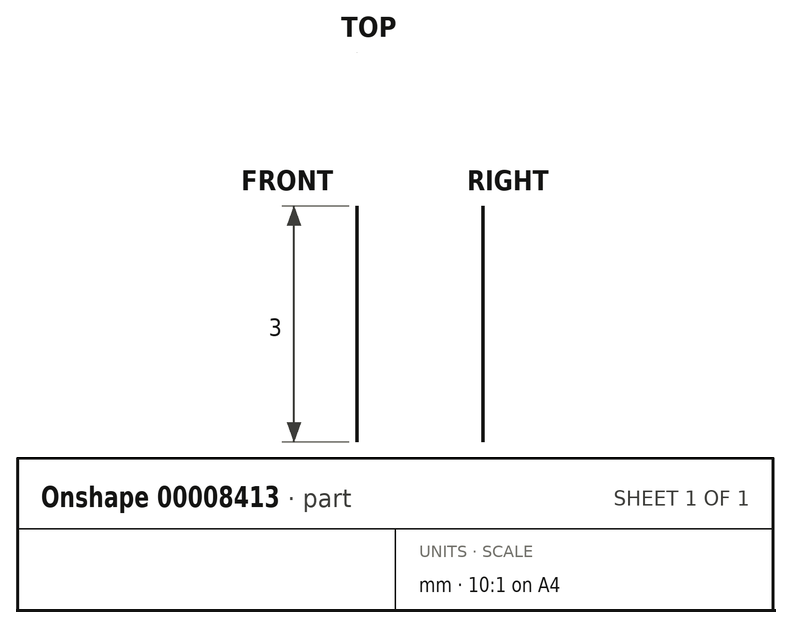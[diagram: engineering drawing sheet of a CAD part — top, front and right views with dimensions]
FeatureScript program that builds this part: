
annotation { "Feature Type Name" : "Feature", "Feature Type Description" : "" }
export const myFeature = defineFeature(function(context is Context, id is Id, definition is map)
    precondition{}
    {
        {
            var Q0;
            Q0=qCreatedBy(makeId("Top.planeOp"),FACE);
            var sketch = newSketch(context, id + "F0", { "sketchPlane" : qUnion([Q0])});
            skLineSegment(sketch, "E0.bottom", {"start": v(0, 0.5) * mm, "end": v(5.1, 0.5) * mm});
            skLineSegment(sketch, "E0.top", {"start": v(0, -0.5) * mm, "end": v(5.1, -0.5) * mm});
            skLineSegment(sketch, "E0.left", {"start": v(0, 0.5) * mm, "end": v(0, -0.5) * mm});
            skPoint(sketch, "E1", {"position": v(5.6, 0) * mm});
            skLineSegment(sketch, "E2", {"start": v(5.6, 1) * mm, "end": v(5.6, 1) * mm});
            skLineSegment(sketch, "E3", {"start": v(6.1, 1.5) * mm, "end": v(9.69, 1.5) * mm});
            skLineSegment(sketch, "E4", {"start": v(9.94, 1.25) * mm, "end": v(9.94, 0.75) * mm});
            skLineSegment(sketch, "E5", {"start": v(9.69, 0.5) * mm, "end": v(7.19, 0.5) * mm});
            skLineSegment(sketch, "E6", {"start": v(6.94, 0.25) * mm, "end": v(6.94, -0.25) * mm});
            skLineSegment(sketch, "E7", {"start": v(7.19, -0.5) * mm, "end": v(9.69, -0.5) * mm});
            skLineSegment(sketch, "E8", {"start": v(9.94, -0.75) * mm, "end": v(9.94, -1.25) * mm});
            skLineSegment(sketch, "E9", {"start": v(9.69, -1.5) * mm, "end": v(6.1, -1.5) * mm});
            skLineSegment(sketch, "E10", {"start": v(5.6, -1) * mm, "end": v(5.6, -1) * mm});
            skLineSegment(sketch, "E11", {"start": v(6.94, 0) * mm, "end": v(5.6, 0) * mm, "construction": true});
            skLineSegment(sketch, "E12", {"start": v(5.6, 0.5) * mm, "end": v(5.6, -0.5) * mm, "construction": true});
            skPoint(sketch, "E13.visualSharp", {"position": v(5.6, 0.5) * mm});
            skArc(sketch, "E13.filletArc", {"start": v(5.1, 0.5) * mm, "mid": v(5.45, 0.65) * mm, "end": v(5.6, 1) * mm});
            skPoint(sketch, "E14.visualSharp", {"position": v(5.6, -0.5) * mm});
            skArc(sketch, "E14.filletArc", {"start": v(5.6, -1) * mm, "mid": v(5.45, -0.65) * mm, "end": v(5.1, -0.5) * mm});
            skPoint(sketch, "E15.visualSharp", {"position": v(6.94, 0.5) * mm});
            skArc(sketch, "E15.filletArc", {"start": v(7.19, 0.5) * mm, "mid": v(7.01, 0.43) * mm, "end": v(6.94, 0.25) * mm});
            skPoint(sketch, "E16.visualSharp", {"position": v(6.94, -0.5) * mm});
            skArc(sketch, "E16.filletArc", {"start": v(6.94, -0.25) * mm, "mid": v(7.01, -0.43) * mm, "end": v(7.19, -0.5) * mm});
            skPoint(sketch, "E17.visualSharp", {"position": v(5.6, 1.5) * mm});
            skArc(sketch, "E17.filletArc", {"start": v(6.1, 1.5) * mm, "mid": v(5.74, 1.35) * mm, "end": v(5.6, 1) * mm});
            skPoint(sketch, "E18.visualSharp", {"position": v(5.6, -1.5) * mm});
            skArc(sketch, "E18.filletArc", {"start": v(5.6, -1) * mm, "mid": v(5.74, -1.35) * mm, "end": v(6.1, -1.5) * mm});
            skPoint(sketch, "E19.visualSharp", {"position": v(9.94, -1.5) * mm});
            skArc(sketch, "E19.filletArc", {"start": v(9.69, -1.5) * mm, "mid": v(9.86, -1.43) * mm, "end": v(9.94, -1.25) * mm});
            skPoint(sketch, "E20.visualSharp", {"position": v(9.94, -0.5) * mm});
            skArc(sketch, "E20.filletArc", {"start": v(9.94, -0.75) * mm, "mid": v(9.86, -0.57) * mm, "end": v(9.69, -0.5) * mm});
            skPoint(sketch, "E21.visualSharp", {"position": v(9.94, 0.5) * mm});
            skArc(sketch, "E21.filletArc", {"start": v(9.69, 0.5) * mm, "mid": v(9.86, 0.57) * mm, "end": v(9.94, 0.75) * mm});
            skPoint(sketch, "E22.visualSharp", {"position": v(9.94, 1.5) * mm});
            skArc(sketch, "E22.filletArc", {"start": v(9.94, 1.25) * mm, "mid": v(9.86, 1.43) * mm, "end": v(9.69, 1.5) * mm});
            skSolve(sketch);
        }
        {
            var Q0;
            Q0 = qSketchRegion(id + "F0", true);
            extrude(context, id + "F1", {"entities" : qUnion([Q0]), "depth" : 3 * mm});
        }
    });
